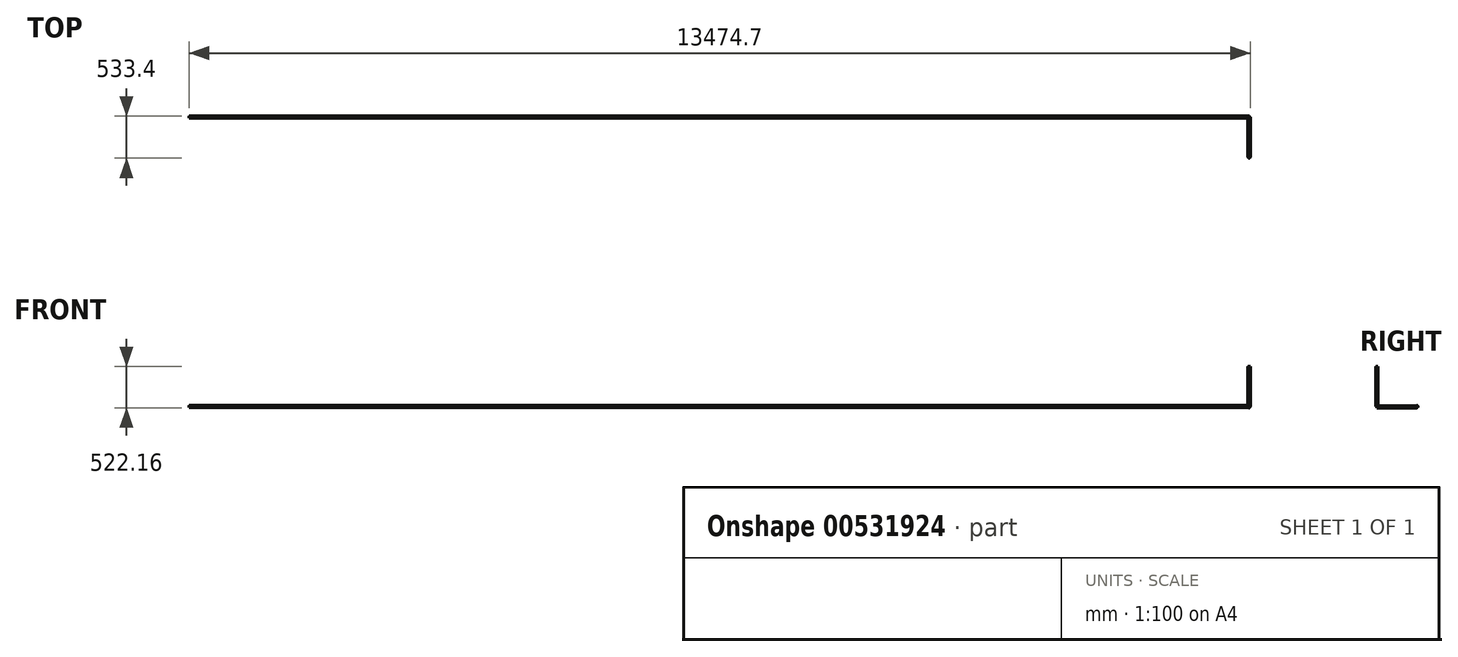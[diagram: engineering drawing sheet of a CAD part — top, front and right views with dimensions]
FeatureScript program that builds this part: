
annotation { "Feature Type Name" : "Feature", "Feature Type Description" : "" }
export const myFeature = defineFeature(function(context is Context, id is Id, definition is map)
    precondition{}
    {
        {
            var Q0;
            Q0=qCreatedBy(makeId("Right.planeOp"),FACE);
            var sketch = newSketch(context, id + "F0", { "sketchPlane" : qUnion([Q0])});
            skCircle(sketch, "E0", {"center": v(0, 0) * mm, "radius": 12.7 * mm});
            skSolve(sketch);
        }
        {
            var Q0;
            Q0 = qSketchRegion(id + "F0", true);
            extrude(context, id + "F1", {"entities" : qUnion([Q0]), "oppositeDirection" : true, "depth" : 13462 * mm, "offsetDistance" : 25.4 * mm});
        }
        {
            var Q0;
            Q0=qCreatedBy(makeId("Front.planeOp"),FACE);
            var sketch = newSketch(context, id + "F2", { "sketchPlane" : qUnion([Q0])});
            skCircle(sketch, "E1", {"center": v(0, -1.46) * mm, "radius": 12.7 * mm});
            skSolve(sketch);
        }
        {
            var Q0;
            Q0 = qSketchRegion(id + "F2", true);
            extrude(context, id + "F3", {"entities" : qUnion([Q0]), "operationType" : NewBodyOperationType.ADD, "depth" : 508 * mm, "offsetDistance" : 25.4 * mm});
        }
        {
            var Q0;
            Q0=makeQuery(id+"F3.opExtrude","CAP_FACE",FACE,{"disambiguationData":[OSD([sQuery(id+"F2.wireOp",EDGE,"E1")])],"isStart":false});
            var sketch = newSketch(context, id + "F4", { "sketchPlane" : qUnion([Q0])});
            skPoint(sketch, "E2", {"position": v(0, -1.46) * mm});
            skSolve(sketch);
        }
        {
            var Q0;
            Q0=qCreatedBy(makeId("Top.planeOp"),FACE);
            var sketch = newSketch(context, id + "F5", { "sketchPlane" : qUnion([Q0])});
            skCircle(sketch, "E3", {"center": v(0, -508) * mm, "radius": 12.7 * mm});
            skSolve(sketch);
        }
        {
            var Q0;
            Q0=makeQuery(id+"F5.imprint","IMPRINT",FACE,{"disambiguationData":[TD([[makeQuery(id+"F5.imprint","IMPRINT",EDGE,{"derivedFrom":sQuery(id+"F5.wireOp",EDGE,"E3")}),1.0]])]});
            extrude(context, id + "F6", {"entities" : qUnion([Q0]), "operationType" : NewBodyOperationType.ADD, "depth" : 508 * mm, "offsetDistance" : 25.4 * mm});
        }
    });
